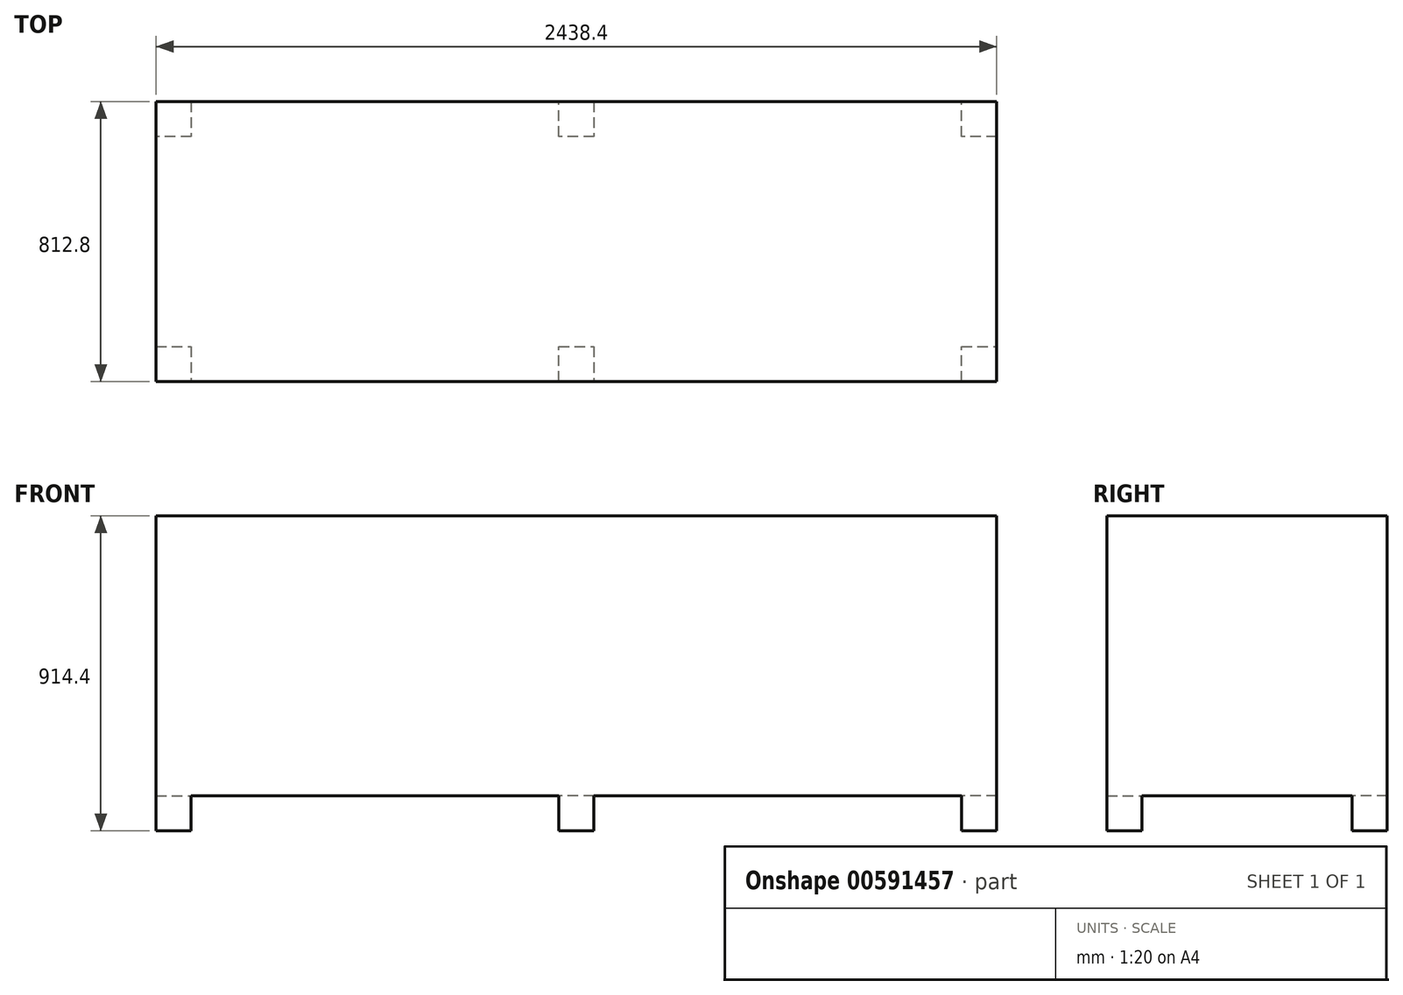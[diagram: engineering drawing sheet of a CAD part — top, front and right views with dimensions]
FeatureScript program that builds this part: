
annotation { "Feature Type Name" : "Feature", "Feature Type Description" : "" }
export const myFeature = defineFeature(function(context is Context, id is Id, definition is map)
    precondition{}
    {
        {
            var Q0;
            Q0=qCreatedBy(makeId("Top.planeOp"),FACE);
            var sketch = newSketch(context, id + "F0", { "sketchPlane" : qUnion([Q0])});
            skLineSegment(sketch, "E0.bottom", {"start": v(-1186.35, 441.9) * mm, "end": v(1252.05, 441.9) * mm});
            skLineSegment(sketch, "E0.top", {"start": v(-1186.35, -370.9) * mm, "end": v(1252.05, -370.9) * mm});
            skLineSegment(sketch, "E0.left", {"start": v(-1186.35, 441.9) * mm, "end": v(-1186.35, -370.9) * mm});
            skLineSegment(sketch, "E0.right", {"start": v(1252.05, 441.9) * mm, "end": v(1252.05, -370.9) * mm});
            skSolve(sketch);
        }
        {
            var Q0;
            Q0=makeQuery(id+"F0.imprint","IMPRINT",FACE,{"disambiguationData":[TD([[makeQuery(id+"F0.imprint","IMPRINT",EDGE,{"derivedFrom":sQuery(id+"F0.wireOp",EDGE,"E0.bottom")}),-1.0]])]});
            extrude(context, id + "F1", {"entities" : qUnion([Q0]), "depth" : 914.4 * mm, "offsetDistance" : 25.4 * mm});
        }
        {
            var Q0;
            Q0=makeQuery(id+"F1.opExtrude","CAP_FACE",FACE,{"disambiguationData":[OSD([sQuery(id+"F0.wireOp",EDGE,"E0.bottom"),sQuery(id+"F0.wireOp",EDGE,"E0.top"),sQuery(id+"F0.wireOp",EDGE,"E0.left"),sQuery(id+"F0.wireOp",EDGE,"E0.right")])],"isStart":true});
            var sketch = newSketch(context, id + "F2", { "sketchPlane" : qUnion([Q0])});
            skLineSegment(sketch, "E1", {"start": v(-1186.35, 269.3) * mm, "end": v(-1084.75, 269.3) * mm});
            skLineSegment(sketch, "E2", {"start": v(-1084.75, 269.3) * mm, "end": v(-1084.75, 370.9) * mm});
            skLineSegment(sketch, "E3", {"start": v(-1084.75, 370.9) * mm, "end": v(-17.95, 370.9) * mm});
            skLineSegment(sketch, "E4", {"start": v(-17.95, 370.9) * mm, "end": v(-17.95, 269.3) * mm});
            skLineSegment(sketch, "E5", {"start": v(-17.95, 269.3) * mm, "end": v(83.65, 269.3) * mm});
            skLineSegment(sketch, "E6", {"start": v(83.65, 269.3) * mm, "end": v(83.65, 370.9) * mm});
            skLineSegment(sketch, "E7", {"start": v(83.65, 370.9) * mm, "end": v(1150.45, 370.9) * mm});
            skLineSegment(sketch, "E8", {"start": v(1150.45, 370.9) * mm, "end": v(1150.45, 269.3) * mm});
            skLineSegment(sketch, "E9", {"start": v(1150.45, 269.3) * mm, "end": v(1252.05, 269.3) * mm});
            skLineSegment(sketch, "E10", {"start": v(1252.05, 269.3) * mm, "end": v(1252.05, -340.3) * mm});
            skLineSegment(sketch, "E11", {"start": v(1252.05, -340.3) * mm, "end": v(1150.45, -340.3) * mm});
            skLineSegment(sketch, "E12", {"start": v(1150.45, -340.3) * mm, "end": v(1150.45, -441.9) * mm});
            skLineSegment(sketch, "E13", {"start": v(1150.45, -441.9) * mm, "end": v(83.65, -441.9) * mm});
            skLineSegment(sketch, "E14", {"start": v(83.65, -441.9) * mm, "end": v(83.65, -340.3) * mm});
            skLineSegment(sketch, "E15", {"start": v(83.65, -340.3) * mm, "end": v(-17.95, -340.3) * mm});
            skPoint(sketch, "E15.endSnap0", {"position": v(-17.95, 320.1) * mm});
            skLineSegment(sketch, "E16", {"start": v(-17.95, -340.3) * mm, "end": v(-17.95, -441.9) * mm});
            skLineSegment(sketch, "E17", {"start": v(-17.95, -441.9) * mm, "end": v(-1084.75, -441.9) * mm});
            skLineSegment(sketch, "E18", {"start": v(-1084.75, -441.9) * mm, "end": v(-1084.75, -340.3) * mm});
            skLineSegment(sketch, "E19", {"start": v(-1084.75, -340.3) * mm, "end": v(-1186.35, -340.3) * mm});
            skLineSegment(sketch, "E20", {"start": v(-1186.35, -340.3) * mm, "end": v(-1186.35, 269.3) * mm});
            skSolve(sketch);
        }
        {
            var Q0;
            Q0 = qSketchRegion(id + "F2", true);
            extrude(context, id + "F3", {"entities" : qUnion([Q0]), "operationType" : NewBodyOperationType.REMOVE, "oppositeDirection" : true, "depth" : 101.6 * mm, "offsetDistance" : 25.4 * mm});
        }
    });
